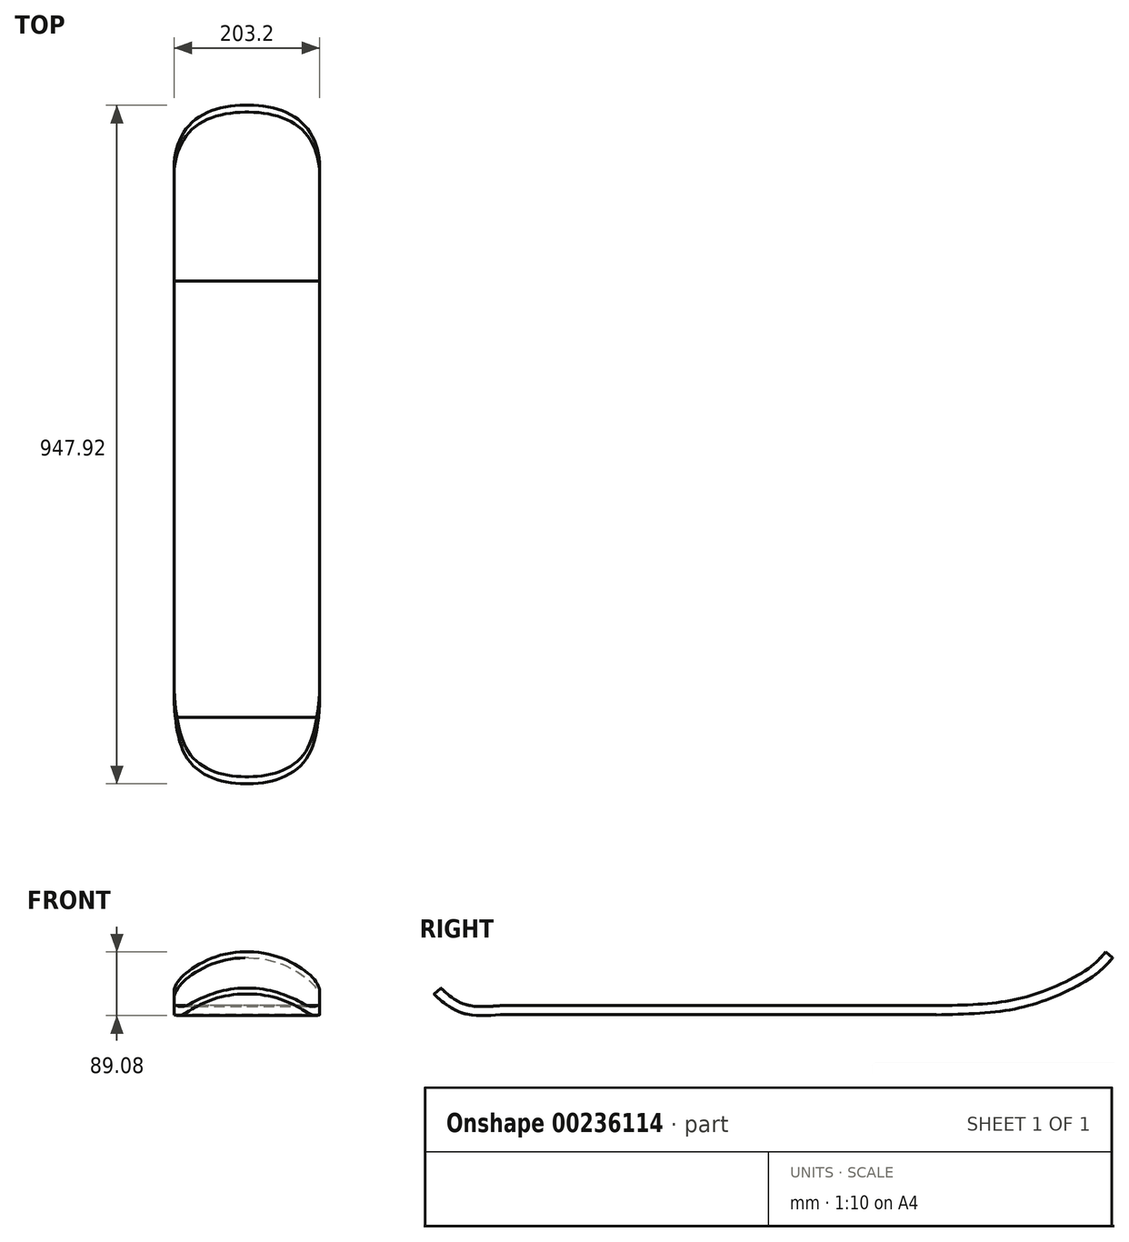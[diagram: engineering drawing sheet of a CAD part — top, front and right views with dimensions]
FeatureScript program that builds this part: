
annotation { "Feature Type Name" : "Feature", "Feature Type Description" : "" }
export const myFeature = defineFeature(function(context is Context, id is Id, definition is map)
    precondition{}
    {
        {
            var Q0;
            Q0=qCreatedBy(makeId("Top.planeOp"),FACE);
            var sketch = newSketch(context, id + "F0", { "sketchPlane" : qUnion([Q0])});
            skLineSegment(sketch, "E0.bottom", {"start": v(101.6, 304.8) * mm, "end": v(-101.6, 304.8) * mm});
            skLineSegment(sketch, "E0.top", {"start": v(101.6, -304.8) * mm, "end": v(-101.6, -304.8) * mm});
            skLineSegment(sketch, "E0.left", {"start": v(101.6, 304.8) * mm, "end": v(101.6, -304.8) * mm});
            skLineSegment(sketch, "E0.right", {"start": v(-101.6, 304.8) * mm, "end": v(-101.6, -304.8) * mm});
            skPoint(sketch, "E0.middle", {"position": v(0, 0) * mm});
            skSolve(sketch);
        }
        {
            var Q0;
            Q0 = qSketchRegion(id + "F0", true);
            extrude(context, id + "F1", {"entities" : qUnion([Q0]), "endBound" : BoundingType.SYMMETRIC, "depth" : 12.7 * mm});
        }
        {
            var Q0;
            Q0=qCreatedBy(makeId("Right.planeOp"),FACE);
            var sketch = newSketch(context, id + "F2", { "sketchPlane" : qUnion([Q0])});
            skFitSpline(sketch, "E1", {"points": [v(304.04, 0) * mm, v(396.5, 5.33) * mm, v(464.06, 23.7) * mm, v(523.75, 55.45) * mm, v(545.67, 77.38) * mm], "startDerivative": vector(319.69, 6.78) * mm, "endDerivative": vector(102.86, 123.33) * mm});
            skFitSpline(sketch, "E2", {"points": [v(-304.81, 0) * mm, v(-347.03, 0) * mm, v(-372.36, 9.98) * mm, v(-387.41, 21.73) * mm, v(-392.55, 26.87) * mm], "startDerivative": vector(-129.66, -9) * mm, "endDerivative": vector(-30.83, 32.45) * mm});
            skSolve(sketch);
        }
        {
            var Q0;
            Q0=makeQuery(id+"F1.opExtrude","SWEPT_FACE",FACE,{"disambiguationData":[OSD([sQuery(id+"F0.wireOp",EDGE,"E0.bottom")])]});
            var Q1;
            Q1=sQuery(id+"F2.wireOp",EDGE,"E1");
            sweep(context, id + "F3", {"operationType" : NewBodyOperationType.ADD, "profiles" : qUnion([Q0]), "path" : qUnion([Q1])});
        }
        {
            var Q0;
            Q0=makeQuery(id+"F1.opExtrude","SWEPT_FACE",FACE,{"disambiguationData":[OSD([sQuery(id+"F0.wireOp",EDGE,"E0.top")])]});
            var Q1;
            Q1=sQuery(id+"F2.wireOp",EDGE,"E2");
            sweep(context, id + "F4", {"operationType" : NewBodyOperationType.ADD, "profiles" : qUnion([Q0]), "path" : qUnion([Q1])});
        }
        {
            var Q0;
            Q0=makeQuery(id+"F4.opSweep","CAP_EDGE",EDGE,{"disambiguationData":[OSD([sQuery(id+"F0.wireOp",EDGE,"E0.top"),sQuery(id+"F0.wireOp",EDGE,"E0.left"),sQuery(id+"F2.wireOp",VERTEX,"E2.end")])],"isStart":false});
            var Q1;
            Q1=makeQuery(id+"F3.opSweep","CAP_EDGE",EDGE,{"disambiguationData":[OSD([sQuery(id+"F0.wireOp",EDGE,"E0.bottom"),sQuery(id+"F0.wireOp",EDGE,"E0.left"),sQuery(id+"F2.wireOp",VERTEX,"E1.end")])],"isStart":false});
            var Q2;
            Q2=makeQuery(id+"F3.opSweep","CAP_EDGE",EDGE,{"disambiguationData":[OSD([sQuery(id+"F0.wireOp",EDGE,"E0.bottom"),sQuery(id+"F0.wireOp",EDGE,"E0.right"),sQuery(id+"F2.wireOp",VERTEX,"E1.end")])],"isStart":false});
            var Q3;
            Q3=makeQuery(id+"F4.opSweep","CAP_EDGE",EDGE,{"disambiguationData":[OSD([sQuery(id+"F0.wireOp",EDGE,"E0.top"),sQuery(id+"F0.wireOp",EDGE,"E0.right"),sQuery(id+"F2.wireOp",VERTEX,"E2.end")])],"isStart":false});
            fillet(context, id + "F5", {"entities" : qUnion([Q0, Q1, Q2, Q3]), "radius" : 99.34 * mm, "tangentPropagation" : true, "allowEdgeOverflow" : false});
        }
    });
